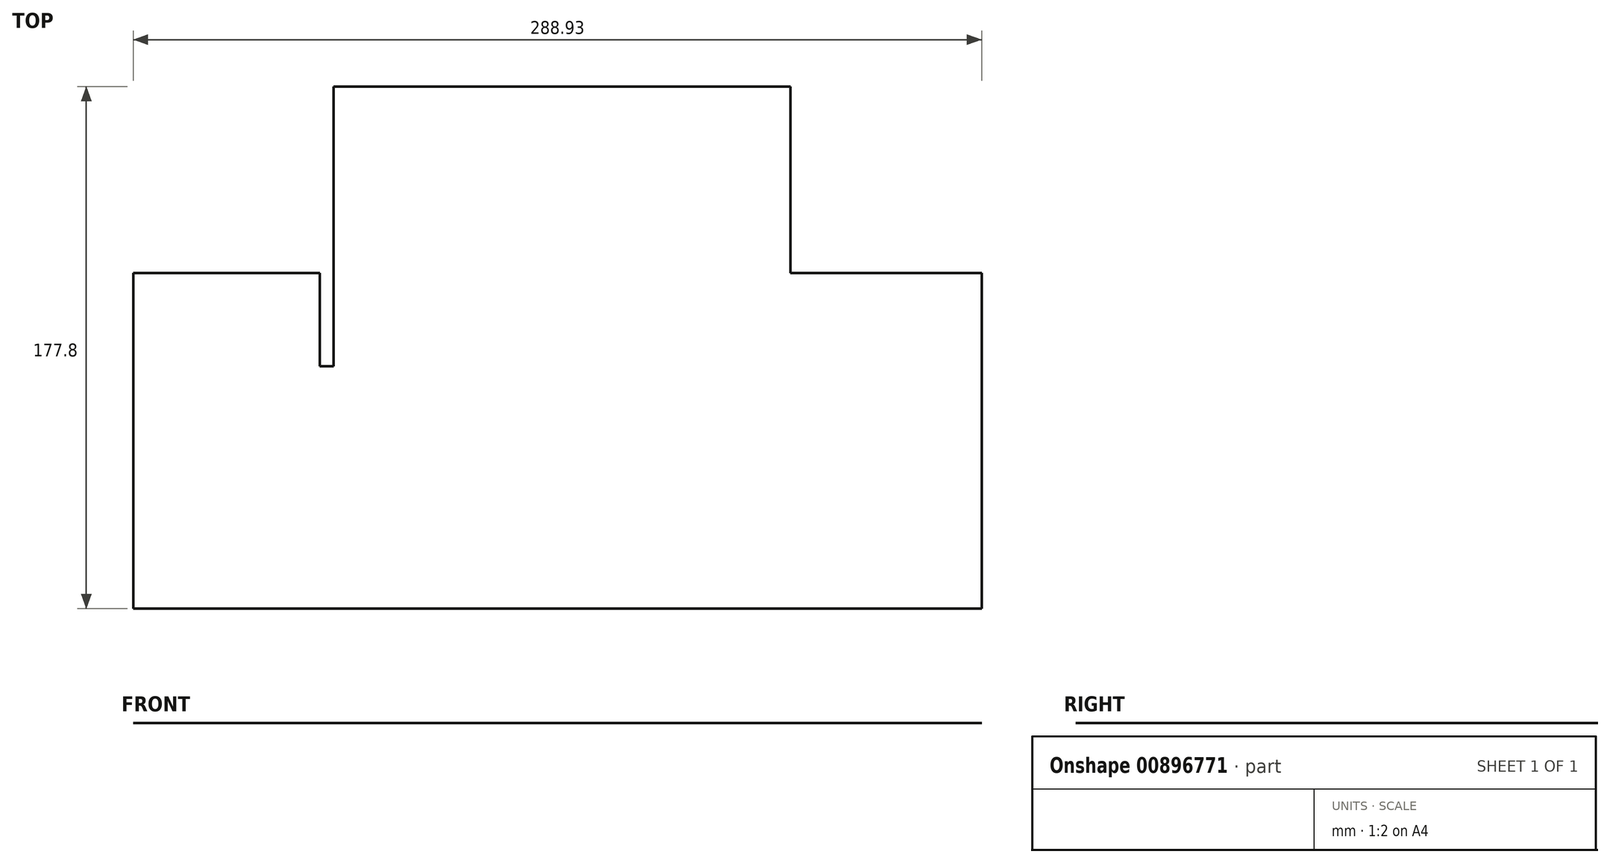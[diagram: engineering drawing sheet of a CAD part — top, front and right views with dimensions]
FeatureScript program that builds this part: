
annotation { "Feature Type Name" : "Feature", "Feature Type Description" : "" }
export const myFeature = defineFeature(function(context is Context, id is Id, definition is map)
    precondition{}
    {
        {
            var Q0;
            Q0=qCreatedBy(makeId("Top.planeOp"),FACE);
            var sketch = newSketch(context, id + "F0", { "sketchPlane" : qUnion([Q0])});
            skLineSegment(sketch, "E0", {"start": v(-135.5, 0) * mm, "end": v(-72, 0) * mm});
            skLineSegment(sketch, "E1", {"start": v(-72, 0) * mm, "end": v(-72, -31.75) * mm});
            skLineSegment(sketch, "E2", {"start": v(-72, -31.75) * mm, "end": v(-67.24, -31.75) * mm});
            skLineSegment(sketch, "E3", {"start": v(-67.24, -31.75) * mm, "end": v(-67.24, 63.5) * mm});
            skLineSegment(sketch, "E4", {"start": v(-67.24, 63.5) * mm, "end": v(88.34, 63.5) * mm});
            skLineSegment(sketch, "E5", {"start": v(88.34, 63.5) * mm, "end": v(88.34, 0) * mm});
            skLineSegment(sketch, "E6", {"start": v(88.34, 0) * mm, "end": v(153.43, 0) * mm});
            skLineSegment(sketch, "E7", {"start": v(153.43, 0) * mm, "end": v(153.43, -114.3) * mm});
            skLineSegment(sketch, "E8", {"start": v(153.43, -114.3) * mm, "end": v(-135.5, -114.3) * mm});
            skLineSegment(sketch, "E9", {"start": v(-135.5, -114.3) * mm, "end": v(-135.5, 0) * mm});
            skSolve(sketch);
        }
        {
            var Q0;
            Q0 = qSketchRegion(id + "F0", true);
            extrude(context, id + "F1", {"entities" : qUnion([Q0]), "depth" : 1 / 203.2 * mm, "offsetDistance" : 25.4 * mm, "symmetric" : true});
        }
    });
